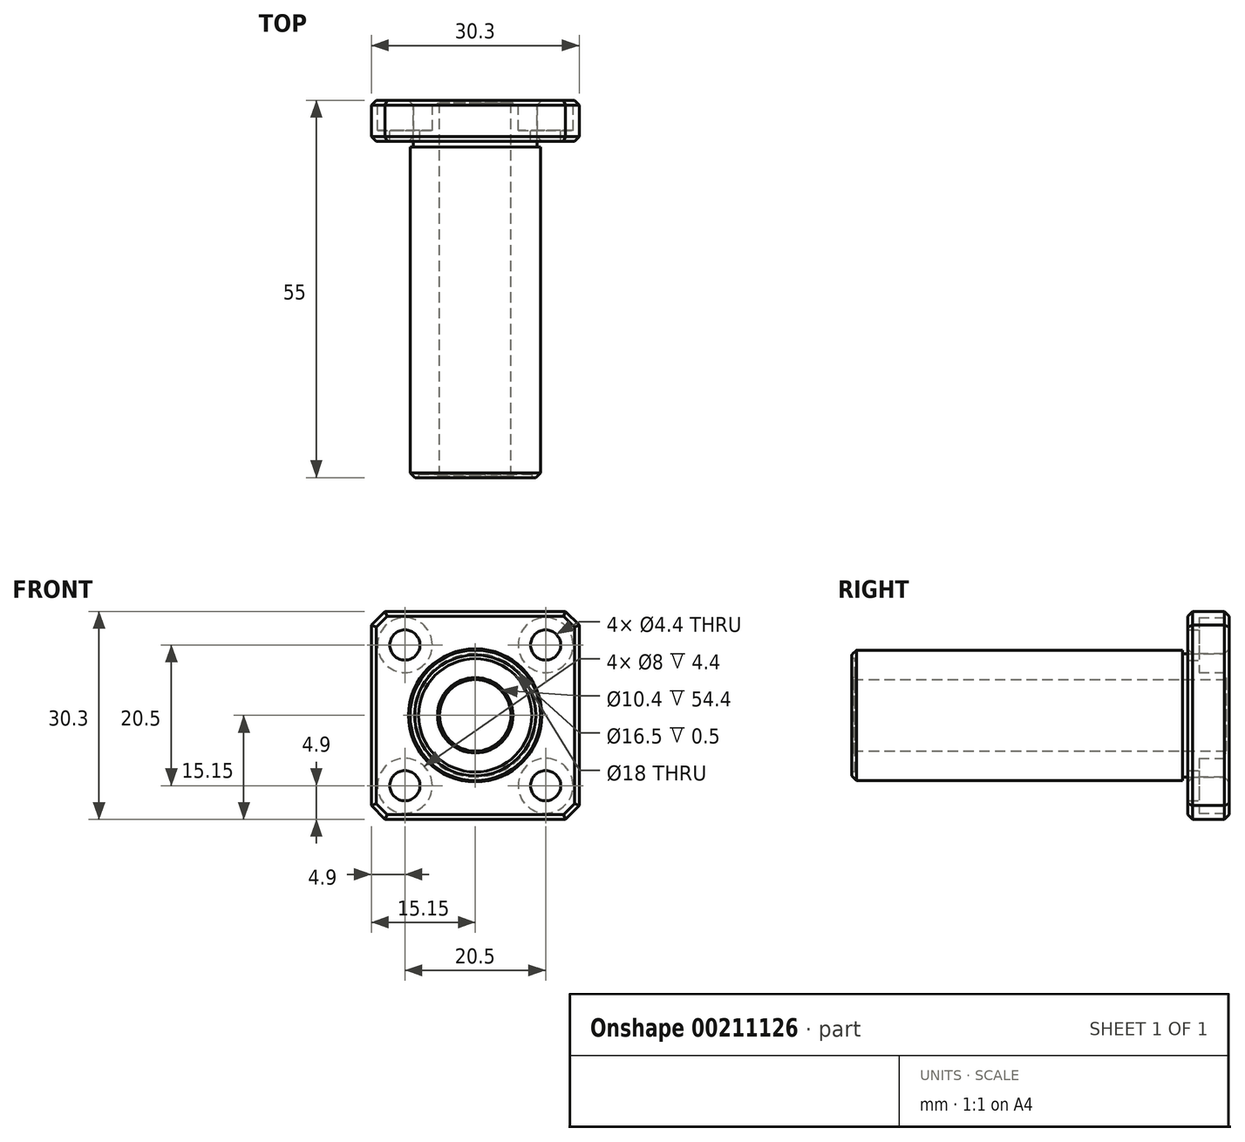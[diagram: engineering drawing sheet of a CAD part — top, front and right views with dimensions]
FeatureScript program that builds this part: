
annotation { "Feature Type Name" : "Feature", "Feature Type Description" : "" }
export const myFeature = defineFeature(function(context is Context, id is Id, definition is map)
    precondition{}
    {
        {
            var Q0;
            Q0=qCreatedBy(makeId("Front.planeOp"),FACE);
            var sketch = newSketch(context, id + "F0", { "sketchPlane" : qUnion([Q0])});
            skCircle(sketch, "E0", {"center": v(0, 0) * mm, "radius": 20 * mm, "construction": true});
            skCircle(sketch, "E1", {"center": v(0, 0) * mm, "radius": 9 * mm});
            skLineSegment(sketch, "E2.bottom", {"start": v(-15.15, 15.15) * mm, "end": v(15.15, 15.15) * mm});
            skLineSegment(sketch, "E2.top", {"start": v(-15.15, -15.15) * mm, "end": v(15.15, -15.15) * mm});
            skLineSegment(sketch, "E2.left", {"start": v(-15.15, 15.15) * mm, "end": v(-15.15, -15.15) * mm});
            skLineSegment(sketch, "E2.right", {"start": v(15.15, 15.15) * mm, "end": v(15.15, -15.15) * mm});
            skLineSegment(sketch, "E3", {"start": v(-15.15, 15.15) * mm, "end": v(15.15, -15.15) * mm, "construction": true});
            skSolve(sketch);
        }
        {
            var Q0;
            Q0=makeQuery(id+"F0.imprint","IMPRINT",FACE,{"disambiguationData":[TD([[makeQuery(id+"F0.imprint","IMPRINT",EDGE,{"derivedFrom":sQuery(id+"F0.wireOp",EDGE,"E0")}),1.0]])]});
            var Q1;
            Q1=makeQuery(id+"F0.imprint","IMPRINT",FACE,{"disambiguationData":[TD([[makeQuery(id+"F0.imprint","IMPRINT",EDGE,{"derivedFrom":sQuery(id+"F0.wireOp",EDGE,"E1")}),-1.0]])]});
            extrude(context, id + "F1", {"entities" : qUnion([Q0, Q1]), "oppositeDirection" : true, "depth" : 6 * mm});
        }
        {
            var Q0;
            Q0=qCreatedBy(makeId("Top.planeOp"),FACE);
            var sketch = newSketch(context, id + "F2", { "sketchPlane" : qUnion([Q0])});
            skLineSegment(sketch, "E4", {"start": v(0, 6) * mm, "end": v(0, -49) * mm});
            skLineSegment(sketch, "E5", {"start": v(0, -49) * mm, "end": v(-9.5, -49) * mm});
            skLineSegment(sketch, "E6", {"start": v(-9.5, -49) * mm, "end": v(-9.5, -0.8) * mm});
            skLineSegment(sketch, "E7", {"start": v(-9.5, -0.8) * mm, "end": v(-9, -0.8) * mm});
            skLineSegment(sketch, "E8", {"start": v(-9, -0.8) * mm, "end": v(-9, 6) * mm});
            skLineSegment(sketch, "E9", {"start": v(-9, 6) * mm, "end": v(0, 6) * mm});
            skLineSegment(sketch, "E10", {"start": v(0, 24.72) * mm, "end": v(0, 6) * mm, "construction": true});
            skSolve(sketch);
        }
        {
            var Q0;
            Q0=makeQuery(id+"F1.opExtrude","SWEPT_EDGE",EDGE,{"disambiguationData":[OSD([sQuery(id+"F0.wireOp",EDGE,"E2.bottom"),sQuery(id+"F0.wireOp",EDGE,"E2.right")])]});
            var Q1;
            Q1=makeQuery(id+"F1.opExtrude","SWEPT_EDGE",EDGE,{"disambiguationData":[OSD([sQuery(id+"F0.wireOp",EDGE,"E2.bottom"),sQuery(id+"F0.wireOp",EDGE,"E2.left")])]});
            var Q2;
            Q2=makeQuery(id+"F1.opExtrude","SWEPT_EDGE",EDGE,{"disambiguationData":[OSD([sQuery(id+"F0.wireOp",EDGE,"E2.top"),sQuery(id+"F0.wireOp",EDGE,"E2.right")])]});
            var Q3;
            Q3=makeQuery(id+"F1.opExtrude","SWEPT_EDGE",EDGE,{"disambiguationData":[OSD([sQuery(id+"F0.wireOp",EDGE,"E2.top"),sQuery(id+"F0.wireOp",EDGE,"E2.left")])]});
            chamfer(context, id + "F3", {"entities" : qUnion([Q0, Q1, Q2, Q3]), "width" : 2 * mm, "tangentPropagation" : true});
        }
        {
            var Q0;
            Q0=makeQuery(id+"F2.imprint","IMPRINT",FACE,{"disambiguationData":[TD([[makeQuery(id+"F2.imprint","IMPRINT",EDGE,{"derivedFrom":sQuery(id+"F2.wireOp",EDGE,"E4")}),-1.0]])]});
            var Q1;
            Q1=sQuery(id+"F2.wireOp",EDGE,"E10");
            revolve(context, id + "F4", {"entities" : qUnion([Q0]), "axis" : qUnion([Q1]), "revolveType" : RevolveType.FULL});
        }
        {
            var Q0;
            Q0=makeQuery(id+"F1.opExtrude","SWEPT_FACE",FACE,{"disambiguationData":[OSD([sQuery(id+"F0.wireOp",EDGE,"E0")])]});
            var Q1;
            Q1=makeQuery(id+"F1.opExtrude","SWEPT_FACE",FACE,{"disambiguationData":[OSD([sQuery(id+"F0.wireOp",EDGE,"E1")])]});
            var Q2;
            Q2=makeQuery(id+"F1.opExtrude","CAP_EDGE",EDGE,{"disambiguationData":[OSD([sQuery(id+"F0.wireOp",EDGE,"E2.bottom")])],"isStart":true});
            var Q3;
            {var subQ0=sQuery(id+"F0.wireOp",EDGE,"E2.left");var subQ1=sQuery(id+"F0.wireOp",EDGE,"E2.bottom");Q3=makeQuery(id+"F3.opChamfer","BLEND_EDGE",EDGE,{"blendedFrom":[makeQuery(id+"F1.opExtrude","SWEPT_EDGE",EDGE,{"disambiguationData":[OSD([subQ1,subQ0])]}),makeQuery(id+"F1.opExtrude","CAP_FACE",FACE,{"disambiguationData":[OSD([sQuery(id+"F0.wireOp",EDGE,"E1"),subQ1,sQuery(id+"F0.wireOp",EDGE,"E2.top"),subQ0,sQuery(id+"F0.wireOp",EDGE,"E2.right")])],"isStart":true})],"blendedInto":[makeQuery(id+"F1.opExtrude","CAP_FACE",FACE,{"disambiguationData":[OSD([sQuery(id+"F0.wireOp",EDGE,"E1"),subQ1,sQuery(id+"F0.wireOp",EDGE,"E2.top"),subQ0,sQuery(id+"F0.wireOp",EDGE,"E2.right")])],"isStart":true})]});}
            var Q4;
            Q4=makeQuery(id+"F1.opExtrude","CAP_EDGE",EDGE,{"disambiguationData":[OSD([sQuery(id+"F0.wireOp",EDGE,"E2.left")])],"isStart":true});
            var Q5;
            {var subQ0=sQuery(id+"F0.wireOp",EDGE,"E2.left");var subQ1=sQuery(id+"F0.wireOp",EDGE,"E2.top");Q5=makeQuery(id+"F3.opChamfer","BLEND_EDGE",EDGE,{"blendedFrom":[makeQuery(id+"F1.opExtrude","SWEPT_EDGE",EDGE,{"disambiguationData":[OSD([subQ1,subQ0])]}),makeQuery(id+"F1.opExtrude","CAP_FACE",FACE,{"disambiguationData":[OSD([sQuery(id+"F0.wireOp",EDGE,"E1"),sQuery(id+"F0.wireOp",EDGE,"E2.bottom"),subQ1,subQ0,sQuery(id+"F0.wireOp",EDGE,"E2.right")])],"isStart":true})],"blendedInto":[makeQuery(id+"F1.opExtrude","CAP_FACE",FACE,{"disambiguationData":[OSD([sQuery(id+"F0.wireOp",EDGE,"E1"),sQuery(id+"F0.wireOp",EDGE,"E2.bottom"),subQ1,subQ0,sQuery(id+"F0.wireOp",EDGE,"E2.right")])],"isStart":true})]});}
            var Q6;
            Q6=makeQuery(id+"F1.opExtrude","CAP_EDGE",EDGE,{"disambiguationData":[OSD([sQuery(id+"F0.wireOp",EDGE,"E2.top")])],"isStart":true});
            var Q7;
            {var subQ0=sQuery(id+"F0.wireOp",EDGE,"E2.right");var subQ1=sQuery(id+"F0.wireOp",EDGE,"E2.top");Q7=makeQuery(id+"F3.opChamfer","BLEND_EDGE",EDGE,{"blendedFrom":[makeQuery(id+"F1.opExtrude","SWEPT_EDGE",EDGE,{"disambiguationData":[OSD([subQ1,subQ0])]}),makeQuery(id+"F1.opExtrude","CAP_FACE",FACE,{"disambiguationData":[OSD([sQuery(id+"F0.wireOp",EDGE,"E1"),sQuery(id+"F0.wireOp",EDGE,"E2.bottom"),subQ1,sQuery(id+"F0.wireOp",EDGE,"E2.left"),subQ0])],"isStart":true})],"blendedInto":[makeQuery(id+"F1.opExtrude","CAP_FACE",FACE,{"disambiguationData":[OSD([sQuery(id+"F0.wireOp",EDGE,"E1"),sQuery(id+"F0.wireOp",EDGE,"E2.bottom"),subQ1,sQuery(id+"F0.wireOp",EDGE,"E2.left"),subQ0])],"isStart":true})]});}
            var Q8;
            Q8=makeQuery(id+"F1.opExtrude","CAP_EDGE",EDGE,{"disambiguationData":[OSD([sQuery(id+"F0.wireOp",EDGE,"E2.right")])],"isStart":true});
            var Q9;
            {var subQ0=sQuery(id+"F0.wireOp",EDGE,"E2.right");var subQ1=sQuery(id+"F0.wireOp",EDGE,"E2.bottom");Q9=makeQuery(id+"F3.opChamfer","BLEND_EDGE",EDGE,{"blendedFrom":[makeQuery(id+"F1.opExtrude","SWEPT_EDGE",EDGE,{"disambiguationData":[OSD([subQ1,subQ0])]}),makeQuery(id+"F1.opExtrude","CAP_FACE",FACE,{"disambiguationData":[OSD([sQuery(id+"F0.wireOp",EDGE,"E1"),subQ1,sQuery(id+"F0.wireOp",EDGE,"E2.top"),sQuery(id+"F0.wireOp",EDGE,"E2.left"),subQ0])],"isStart":true})],"blendedInto":[makeQuery(id+"F1.opExtrude","CAP_FACE",FACE,{"disambiguationData":[OSD([sQuery(id+"F0.wireOp",EDGE,"E1"),subQ1,sQuery(id+"F0.wireOp",EDGE,"E2.top"),sQuery(id+"F0.wireOp",EDGE,"E2.left"),subQ0])],"isStart":true})]});}
            var Q10;
            Q10=makeQuery(id+"F1.opExtrude","CAP_EDGE",EDGE,{"disambiguationData":[OSD([sQuery(id+"F0.wireOp",EDGE,"E2.right")])],"isStart":false});
            var Q11;
            {var subQ0=sQuery(id+"F0.wireOp",EDGE,"E2.right");var subQ1=sQuery(id+"F0.wireOp",EDGE,"E2.bottom");Q11=makeQuery(id+"F3.opChamfer","BLEND_EDGE",EDGE,{"blendedFrom":[makeQuery(id+"F1.opExtrude","SWEPT_EDGE",EDGE,{"disambiguationData":[OSD([subQ1,subQ0])]}),makeQuery(id+"F1.opExtrude","CAP_FACE",FACE,{"disambiguationData":[OSD([sQuery(id+"F0.wireOp",EDGE,"E1"),subQ1,sQuery(id+"F0.wireOp",EDGE,"E2.top"),sQuery(id+"F0.wireOp",EDGE,"E2.left"),subQ0])],"isStart":false})],"blendedInto":[makeQuery(id+"F1.opExtrude","CAP_FACE",FACE,{"disambiguationData":[OSD([sQuery(id+"F0.wireOp",EDGE,"E1"),subQ1,sQuery(id+"F0.wireOp",EDGE,"E2.top"),sQuery(id+"F0.wireOp",EDGE,"E2.left"),subQ0])],"isStart":false})]});}
            var Q12;
            Q12=makeQuery(id+"F1.opExtrude","CAP_EDGE",EDGE,{"disambiguationData":[OSD([sQuery(id+"F0.wireOp",EDGE,"E2.bottom")])],"isStart":false});
            var Q13;
            {var subQ0=sQuery(id+"F0.wireOp",EDGE,"E2.left");var subQ1=sQuery(id+"F0.wireOp",EDGE,"E2.bottom");Q13=makeQuery(id+"F3.opChamfer","BLEND_EDGE",EDGE,{"blendedFrom":[makeQuery(id+"F1.opExtrude","SWEPT_EDGE",EDGE,{"disambiguationData":[OSD([subQ1,subQ0])]}),makeQuery(id+"F1.opExtrude","CAP_FACE",FACE,{"disambiguationData":[OSD([sQuery(id+"F0.wireOp",EDGE,"E1"),subQ1,sQuery(id+"F0.wireOp",EDGE,"E2.top"),subQ0,sQuery(id+"F0.wireOp",EDGE,"E2.right")])],"isStart":false})],"blendedInto":[makeQuery(id+"F1.opExtrude","CAP_FACE",FACE,{"disambiguationData":[OSD([sQuery(id+"F0.wireOp",EDGE,"E1"),subQ1,sQuery(id+"F0.wireOp",EDGE,"E2.top"),subQ0,sQuery(id+"F0.wireOp",EDGE,"E2.right")])],"isStart":false})]});}
            var Q14;
            Q14=makeQuery(id+"F1.opExtrude","CAP_EDGE",EDGE,{"disambiguationData":[OSD([sQuery(id+"F0.wireOp",EDGE,"E2.left")])],"isStart":false});
            var Q15;
            {var subQ0=sQuery(id+"F0.wireOp",EDGE,"E2.left");var subQ1=sQuery(id+"F0.wireOp",EDGE,"E2.top");Q15=makeQuery(id+"F3.opChamfer","BLEND_EDGE",EDGE,{"blendedFrom":[makeQuery(id+"F1.opExtrude","SWEPT_EDGE",EDGE,{"disambiguationData":[OSD([subQ1,subQ0])]}),makeQuery(id+"F1.opExtrude","CAP_FACE",FACE,{"disambiguationData":[OSD([sQuery(id+"F0.wireOp",EDGE,"E1"),sQuery(id+"F0.wireOp",EDGE,"E2.bottom"),subQ1,subQ0,sQuery(id+"F0.wireOp",EDGE,"E2.right")])],"isStart":false})],"blendedInto":[makeQuery(id+"F1.opExtrude","CAP_FACE",FACE,{"disambiguationData":[OSD([sQuery(id+"F0.wireOp",EDGE,"E1"),sQuery(id+"F0.wireOp",EDGE,"E2.bottom"),subQ1,subQ0,sQuery(id+"F0.wireOp",EDGE,"E2.right")])],"isStart":false})]});}
            var Q16;
            Q16=makeQuery(id+"F1.opExtrude","CAP_EDGE",EDGE,{"disambiguationData":[OSD([sQuery(id+"F0.wireOp",EDGE,"E2.top")])],"isStart":false});
            var Q17;
            {var subQ0=sQuery(id+"F0.wireOp",EDGE,"E2.right");var subQ1=sQuery(id+"F0.wireOp",EDGE,"E2.top");Q17=makeQuery(id+"F3.opChamfer","BLEND_EDGE",EDGE,{"blendedFrom":[makeQuery(id+"F1.opExtrude","SWEPT_EDGE",EDGE,{"disambiguationData":[OSD([subQ1,subQ0])]}),makeQuery(id+"F1.opExtrude","CAP_FACE",FACE,{"disambiguationData":[OSD([sQuery(id+"F0.wireOp",EDGE,"E1"),sQuery(id+"F0.wireOp",EDGE,"E2.bottom"),subQ1,sQuery(id+"F0.wireOp",EDGE,"E2.left"),subQ0])],"isStart":false})],"blendedInto":[makeQuery(id+"F1.opExtrude","CAP_FACE",FACE,{"disambiguationData":[OSD([sQuery(id+"F0.wireOp",EDGE,"E1"),sQuery(id+"F0.wireOp",EDGE,"E2.bottom"),subQ1,sQuery(id+"F0.wireOp",EDGE,"E2.left"),subQ0])],"isStart":false})]});}
            chamfer(context, id + "F5", {"entities" : qUnion([Q0, Q1, Q2, Q3, Q4, Q5, Q6, Q7, Q8, Q9, Q10, Q11, Q12, Q13, Q14, Q15, Q16, Q17]), "width" : .7 * mm, "tangentPropagation" : true});
        }
        {
            var Q0;
            Q0=makeQuery(id+"F1.opExtrude","CAP_FACE",FACE,{"disambiguationData":[OSD([sQuery(id+"F0.wireOp",EDGE,"E0"),sQuery(id+"F0.wireOp",EDGE,"E1")])],"isStart":false});
            var sketch = newSketch(context, id + "F6", { "sketchPlane" : qUnion([Q0])});
            skLineSegment(sketch, "E11.bottom", {"start": v(-10.25, 10.25) * mm, "end": v(10.25, 10.25) * mm});
            skLineSegment(sketch, "E11.top", {"start": v(-10.25, -10.25) * mm, "end": v(10.25, -10.25) * mm});
            skLineSegment(sketch, "E11.left", {"start": v(-10.25, 10.25) * mm, "end": v(-10.25, -10.25) * mm});
            skLineSegment(sketch, "E11.right", {"start": v(10.25, 10.25) * mm, "end": v(10.25, -10.25) * mm});
            skLineSegment(sketch, "E12", {"start": v(-10.25, 10.25) * mm, "end": v(10.25, -10.25) * mm});
            skSolve(sketch);
        }
        {
            var Q0;
            Q0=sQuery(id+"F6.wireOp",VERTEX,"E11.left.start");
            var Q1;
            Q1=sQuery(id+"F6.wireOp",VERTEX,"E11.bottom.end");
            var Q2;
            Q2=sQuery(id+"F6.wireOp",VERTEX,"E11.top.end");
            var Q3;
            Q3=sQuery(id+"F6.wireOp",VERTEX,"E11.left.end");
            var Q4;
            Q4=makeQuery(id+"F1.opExtrude","SWEPT_BODY",BODY,{"disambiguationData":[OSD([sQuery(id+"F0.wireOp",EDGE,"E0"),sQuery(id+"F0.wireOp",EDGE,"E1")])]});
            hole(context, id + "F7", {"style" : HoleStyle.C_BORE, "endStyle" : HoleEndStyle.THROUGH, "holeDiameter" : 4.4 * mm, "cBoreDiameter" : 8 * mm, "cBoreDepth" : 4.4 * mm, "locations" : qUnion([Q0, Q1, Q2, Q3]), "scope" : qUnion([Q4]), "isTappedThrough" : true});
        }
        {
            var Q0;
            Q0=makeQuery(id+"F4.opRevolve","SWEPT_EDGE",EDGE,{"disambiguationData":[OSD([sQuery(id+"F2.wireOp",EDGE,"E5"),sQuery(id+"F2.wireOp",EDGE,"E6")])]});
            chamfer(context, id + "F8", {"entities" : qUnion([Q0]), "width" : .7 * mm, "tangentPropagation" : true});
        }
        {
            var Q0;
            Q0=makeQuery(id+"F4.opRevolve","SWEPT_FACE",FACE,{"disambiguationData":[OSD([sQuery(id+"F2.wireOp",EDGE,"E9")])]});
            var sketch = newSketch(context, id + "F9", { "sketchPlane" : qUnion([Q0])});
            skCircle(sketch, "E13", {"center": v(0, 0) * mm, "radius": 9 * mm});
            skCircle(sketch, "E14", {"center": v(0, 0) * mm, "radius": 5.5 * mm});
            skCircle(sketch, "E15", {"center": v(0, 0) * mm, "radius": 5.2 * mm});
            skSolve(sketch);
        }
        {
            var Q0;
            Q0=makeQuery(id+"F9.imprint","IMPRINT",FACE,{"disambiguationData":[TD([[makeQuery(id+"F9.imprint","IMPRINT",EDGE,{"derivedFrom":sQuery(id+"F9.wireOp",EDGE,"E13")}),1.0]])]});
            extrude(context, id + "F10", {"entities" : qUnion([Q0]), "operationType" : NewBodyOperationType.REMOVE, "oppositeDirection" : true, "depth" : .7 * mm});
        }
        {
            var Q0;
            Q0=makeQuery(id+"F9.imprint","IMPRINT",FACE,{"disambiguationData":[TD([[makeQuery(id+"F9.imprint","IMPRINT",EDGE,{"derivedFrom":sQuery(id+"F9.wireOp",EDGE,"E14")}),1.0]])]});
            extrude(context, id + "F11", {"entities" : qUnion([Q0]), "operationType" : NewBodyOperationType.REMOVE, "oppositeDirection" : true, "depth" : .4 * mm});
        }
        {
            var Q0;
            Q0=makeQuery(id+"F9.imprint","IMPRINT",FACE,{"disambiguationData":[TD([[makeQuery(id+"F9.imprint","IMPRINT",EDGE,{"derivedFrom":sQuery(id+"F9.wireOp",EDGE,"E15")}),1.0]])]});
            extrude(context, id + "F12", {"entities" : qUnion([Q0]), "operationType" : NewBodyOperationType.REMOVE, "endBound" : BoundingType.UP_TO_NEXT, "oppositeDirection" : true, "depth" : 25 * mm});
        }
        {
            var Q0;
            Q0=makeQuery(id+"F4.opRevolve","SWEPT_FACE",FACE,{"disambiguationData":[OSD([sQuery(id+"F2.wireOp",EDGE,"E5")])]});
            var sketch = newSketch(context, id + "F13", { "sketchPlane" : qUnion([Q0])});
            skCircle(sketch, "E16", {"center": v(0, 0) * mm, "radius": 8.25 * mm});
            skCircle(sketch, "E17", {"center": v(0, 0) * mm, "radius": 5.5 * mm});
            skCircle(sketch, "E18", {"center": v(0, 0) * mm, "radius": 5.2 * mm});
            skSolve(sketch);
        }
        {
            var Q0;
            Q0=makeQuery(id+"F13.imprint","IMPRINT",FACE,{"disambiguationData":[TD([[makeQuery(id+"F13.imprint","IMPRINT",EDGE,{"derivedFrom":sQuery(id+"F13.wireOp",EDGE,"E16")}),1.0]])]});
            extrude(context, id + "F14", {"entities" : qUnion([Q0]), "operationType" : NewBodyOperationType.REMOVE, "oppositeDirection" : true, "depth" : .5 * mm});
        }
        {
            var Q0;
            Q0=makeQuery(id+"F13.imprint","IMPRINT",FACE,{"disambiguationData":[TD([[makeQuery(id+"F13.imprint","IMPRINT",EDGE,{"derivedFrom":sQuery(id+"F13.wireOp",EDGE,"E17")}),1.0]])]});
            extrude(context, id + "F15", {"entities" : qUnion([Q0]), "operationType" : NewBodyOperationType.REMOVE, "oppositeDirection" : true, "depth" : .2 * mm});
        }
    });
